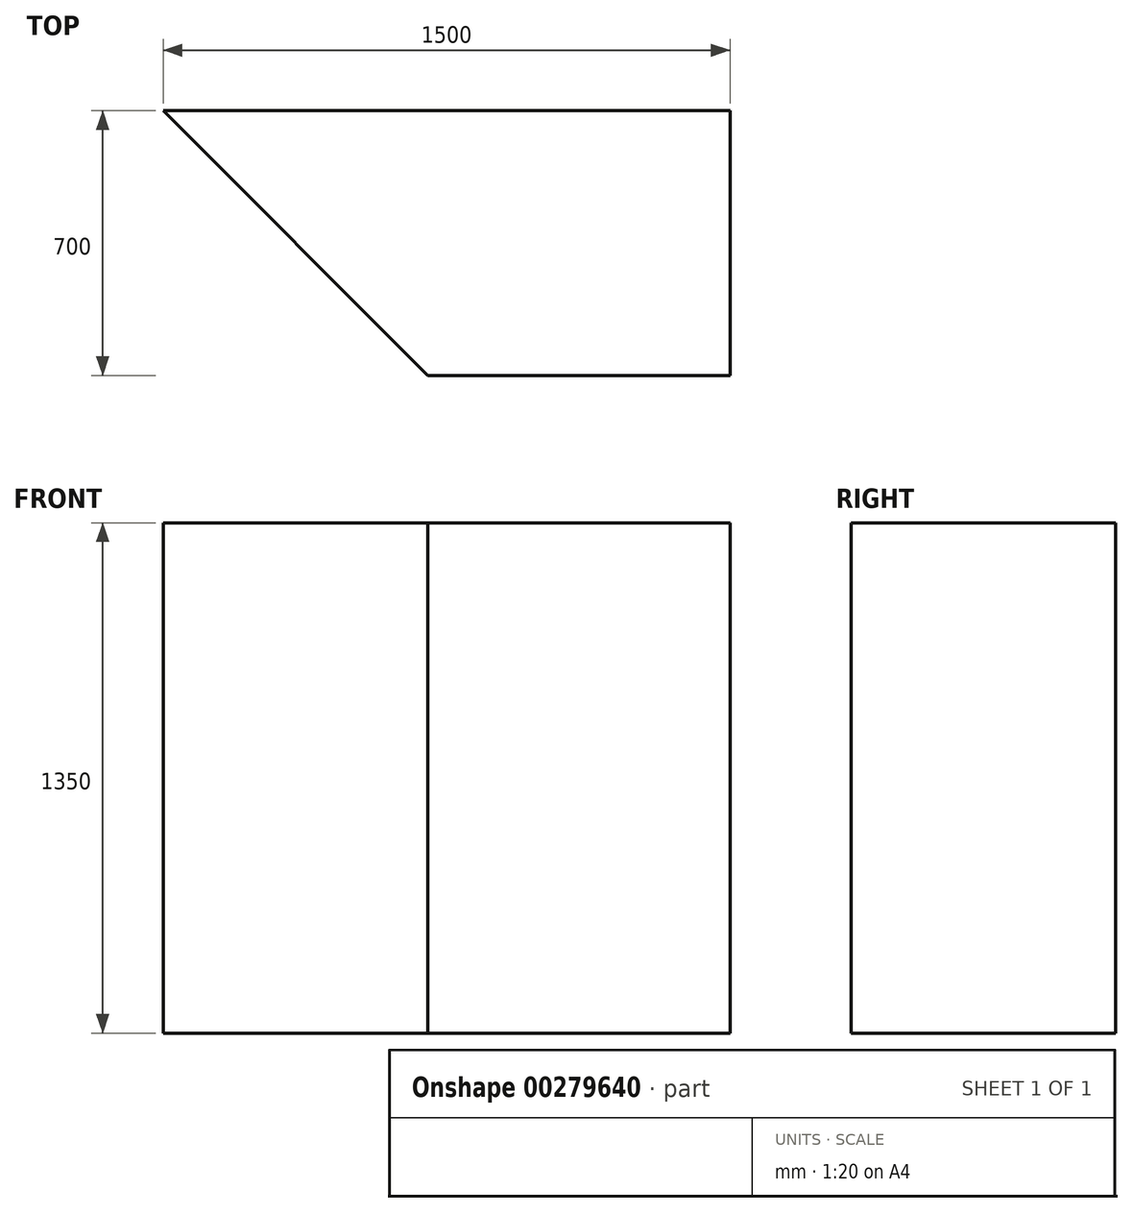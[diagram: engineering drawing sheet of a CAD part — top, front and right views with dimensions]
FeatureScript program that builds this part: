
annotation { "Feature Type Name" : "Feature", "Feature Type Description" : "" }
export const myFeature = defineFeature(function(context is Context, id is Id, definition is map)
    precondition{}
    {
        {
            var Q0;
            Q0=qCreatedBy(makeId("Top.planeOp"),FACE);
            var sketch = newSketch(context, id + "F0", { "sketchPlane" : qUnion([Q0])});
            skLineSegment(sketch, "E0", {"start": v(0, 0) * mm, "end": v(0, 700) * mm});
            skLineSegment(sketch, "E1", {"start": v(0, 700) * mm, "end": v(-1500, 700) * mm});
            skLineSegment(sketch, "E2", {"start": v(-1500, 700) * mm, "end": v(-800, 0) * mm});
            skLineSegment(sketch, "E3", {"start": v(-800, 0) * mm, "end": v(0, 0) * mm});
            skSolve(sketch);
        }
        {
            var Q0;
            Q0=makeQuery(id+"F0.imprint","IMPRINT",FACE,{"disambiguationData":[TD([[makeQuery(id+"F0.imprint","IMPRINT",EDGE,{"derivedFrom":sQuery(id+"F0.wireOp",EDGE,"E0")}),1.0]])]});
            extrude(context, id + "F1", {"entities" : qUnion([Q0]), "depth" : 1350 * mm});
        }
    });
